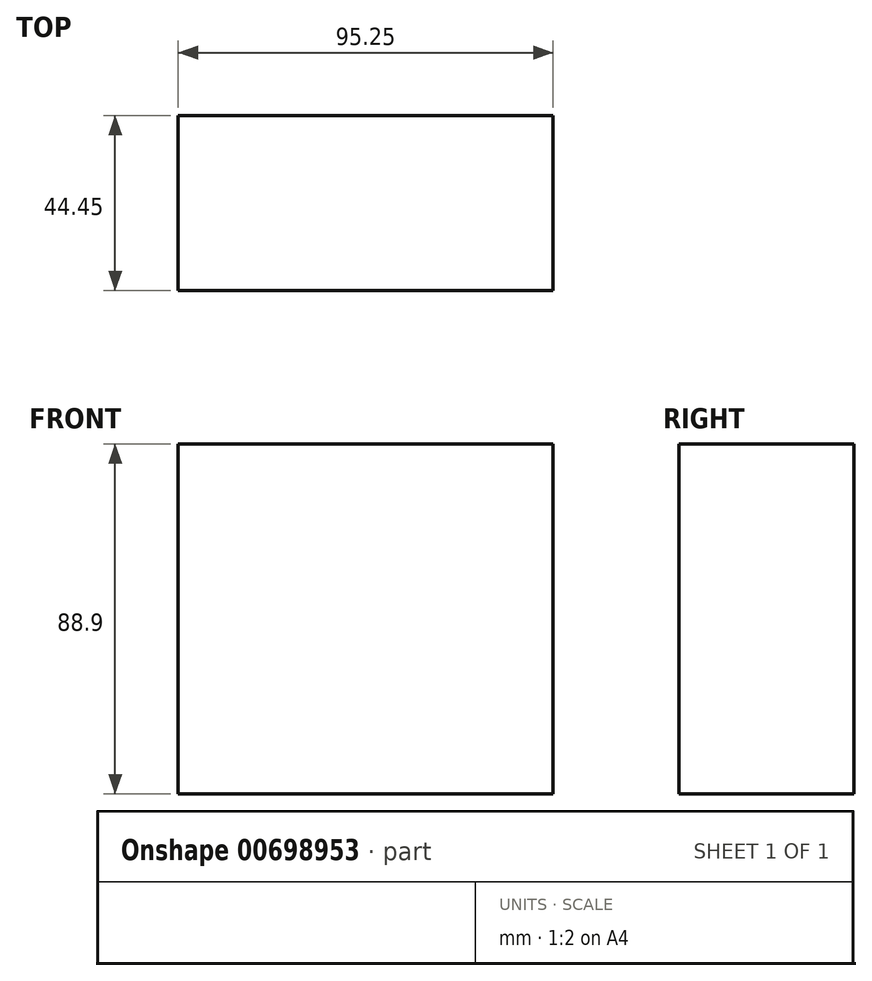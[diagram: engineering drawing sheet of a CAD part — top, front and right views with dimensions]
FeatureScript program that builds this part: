
annotation { "Feature Type Name" : "Feature", "Feature Type Description" : "" }
export const myFeature = defineFeature(function(context is Context, id is Id, definition is map)
    precondition{}
    {
        {
            var Q0;
            Q0=qCreatedBy(makeId("Top.planeOp"),FACE);
            var sketch = newSketch(context, id + "F0", { "sketchPlane" : qUnion([Q0])});
            skLineSegment(sketch, "E0", {"start": v(-97.62, 46) * mm, "end": v(-2.37, 46) * mm});
            skLineSegment(sketch, "E1", {"start": v(-2.37, 46) * mm, "end": v(-2.37, 1.56) * mm});
            skLineSegment(sketch, "E2", {"start": v(-2.37, 1.56) * mm, "end": v(-97.62, 1.56) * mm});
            skLineSegment(sketch, "E3", {"start": v(-97.62, 1.56) * mm, "end": v(-97.62, 46) * mm});
            skSolve(sketch);
        }
        {
            var Q0;
            Q0=makeQuery(id+"F0.imprint","IMPRINT",FACE,{"disambiguationData":[TD([[makeQuery(id+"F0.imprint","IMPRINT",EDGE,{"derivedFrom":sQuery(id+"F0.wireOp",EDGE,"E0")}),-1.0]])]});
            extrude(context, id + "F1", {"entities" : qUnion([Q0]), "depth" : 88.9 * mm, "offsetDistance" : 25.4 * mm});
        }
    });
